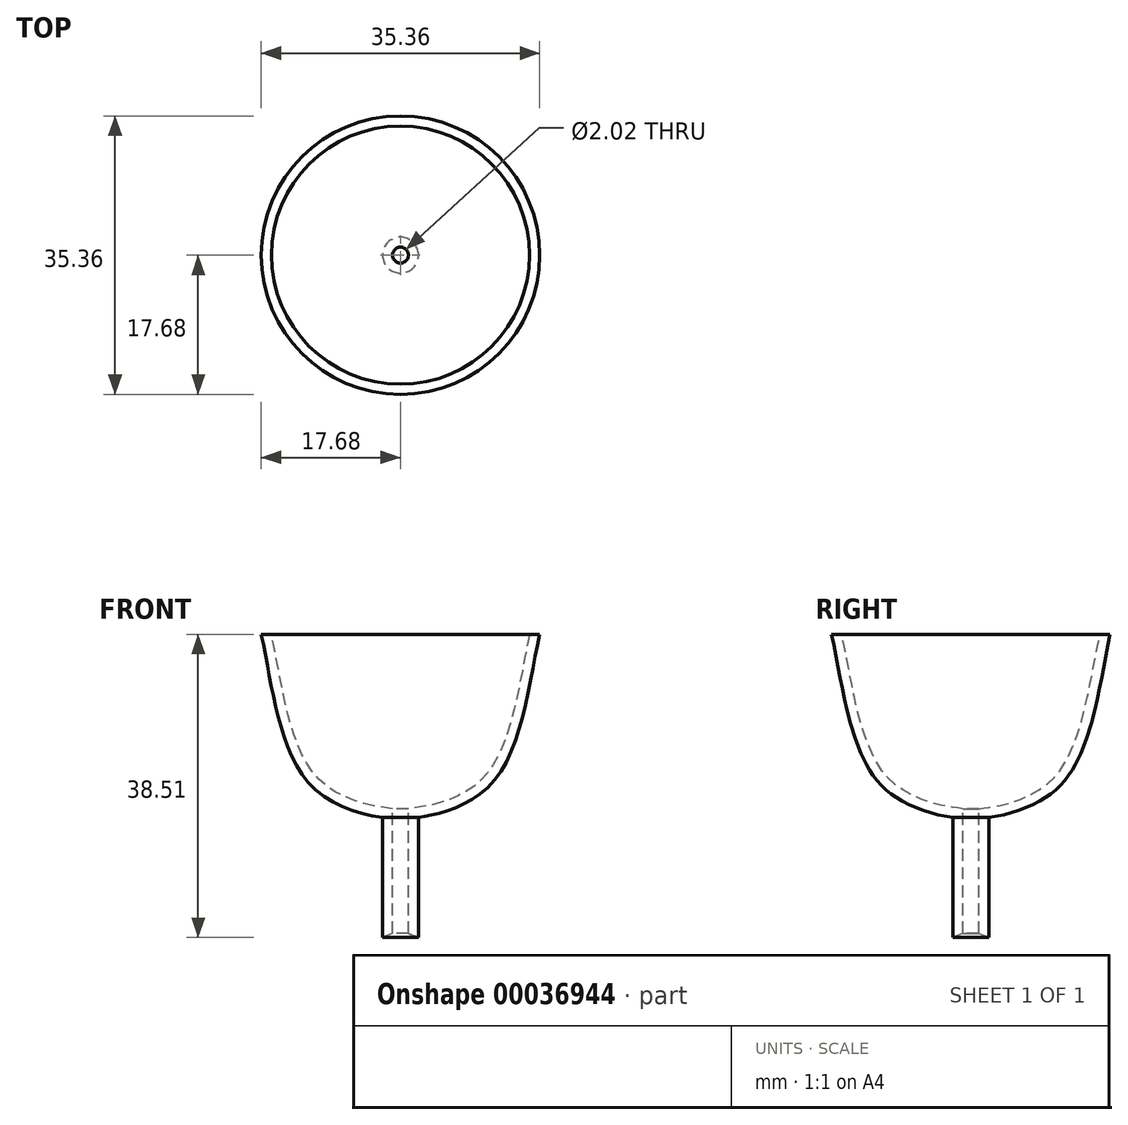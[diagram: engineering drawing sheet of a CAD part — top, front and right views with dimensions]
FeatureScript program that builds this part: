
annotation { "Feature Type Name" : "Feature", "Feature Type Description" : "" }
export const myFeature = defineFeature(function(context is Context, id is Id, definition is map)
    precondition{}
    {
        {
            var Q0;
            Q0=qCreatedBy(makeId("Front.planeOp"),FACE);
            var sketch = newSketch(context, id + "F0", { "sketchPlane" : qUnion([Q0])});
            skLineSegment(sketch, "E0", {"start": v(0, 23.25) * mm, "end": v(0, -20.97) * mm});
            skLineSegment(sketch, "E1", {"start": v(0, -20.97) * mm, "end": v(11.98, -20.97) * mm});
            skLineSegment(sketch, "E2", {"start": v(0, 23.25) * mm, "end": v(17.68, 23.25) * mm});
            skLineSegment(sketch, "E3", {"start": v(2.28, 0) * mm, "end": v(2.28, -15.26) * mm});
            skFitSpline(sketch, "E4", {"points": [v(17.68, 23.25) * mm, v(11.7, 4.42) * mm, v(2.28, 0) * mm, v(0, 0) * mm], "startDerivative": vector(-8.12, -36.69) * mm, "endDerivative": vector(-11.44, 2.75) * mm});
            skFitSpline(sketch, "E5", {"points": [v(2.28, -15.26) * mm, v(7.7, -17.83) * mm, v(11.98, -20.97) * mm], "startDerivative": vector(10.95, -4.6) * mm, "endDerivative": vector(8.42, -6.83) * mm});
            skSolve(sketch);
        }
        {
            var Q0;
            Q0 = qSketchRegion(id + "F0", true);
            var Q1;
            Q1=sQuery(id+"F0.wireOp",EDGE,"E0");
            revolve(context, id + "F1", {"entities" : qUnion([Q0]), "axis" : qUnion([Q1]), "revolveType" : RevolveType.FULL});
        }
        {
            var Q0;
            Q0=makeQuery(id+"F1.opRevolve","SWEPT_FACE",FACE,{"disambiguationData":[OSD([sQuery(id+"F0.wireOp",EDGE,"E2")])]});
            var Q1;
            Q1=makeQuery(id+"F1.opRevolve","SWEPT_FACE",FACE,{"disambiguationData":[OSD([sQuery(id+"F0.wireOp",EDGE,"E5")])]});
            var Q2;
            Q2=makeQuery(id+"F1.opRevolve","SWEPT_FACE",FACE,{"disambiguationData":[OSD([sQuery(id+"F0.wireOp",EDGE,"E1")])]});
            shell(context, id + "F2", {"entities" : qUnion([Q0, Q1, Q2]), "thickness" : 1.27 * mm});
        }
    });
